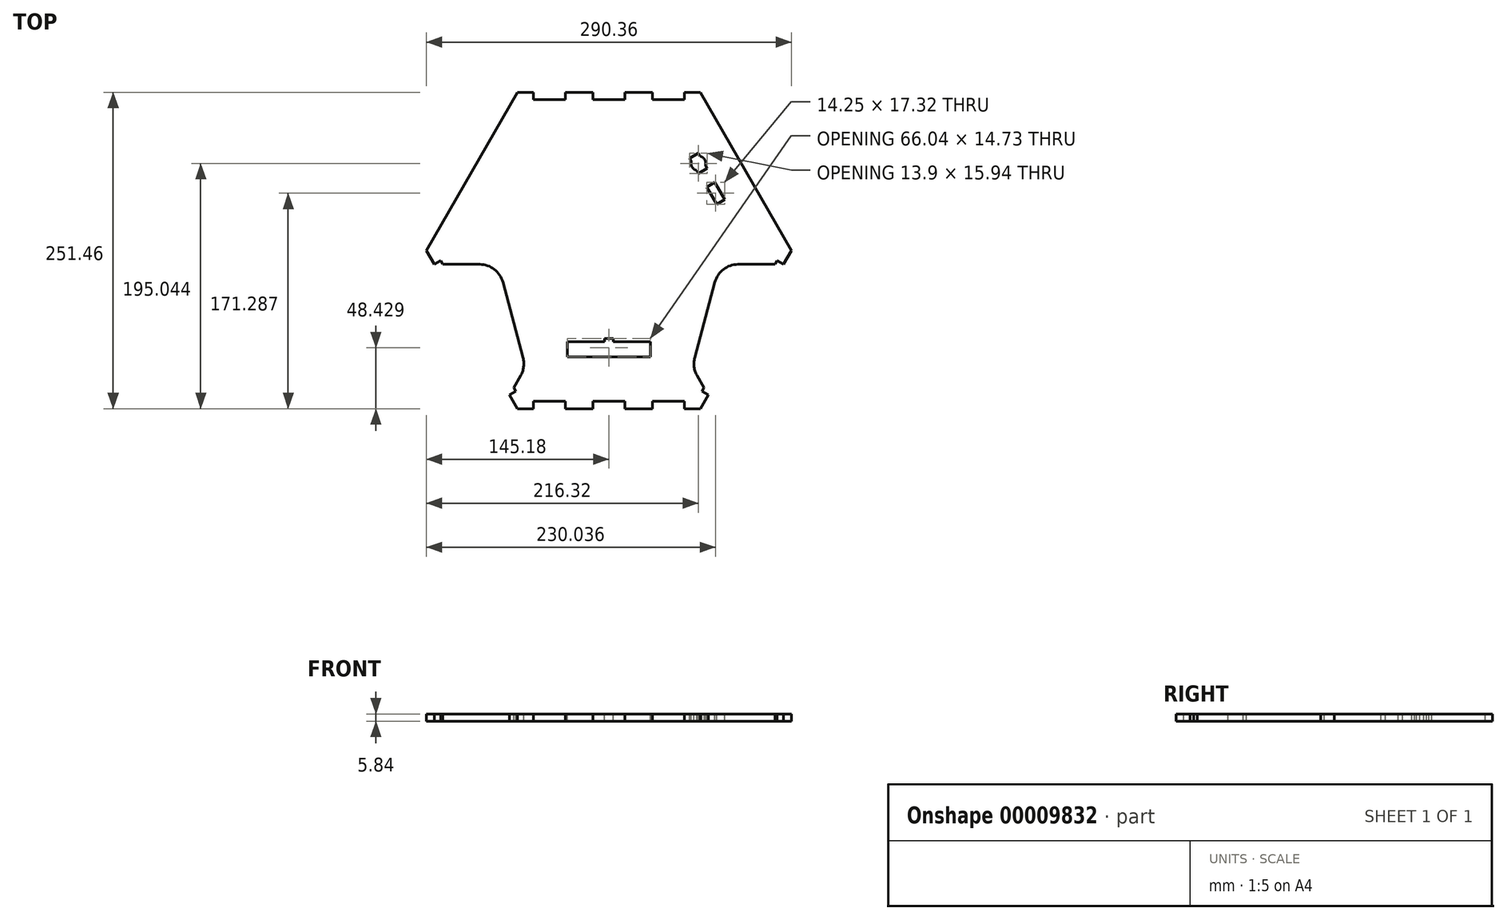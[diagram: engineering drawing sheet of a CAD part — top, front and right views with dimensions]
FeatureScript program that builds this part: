
annotation { "Feature Type Name" : "Feature", "Feature Type Description" : "" }
export const myFeature = defineFeature(function(context is Context, id is Id, definition is map)
    precondition{}
    {
        {
            var Q0;
            Q0=qCreatedBy(makeId("Top.planeOp"),FACE);
            var sketch = newSketch(context, id + "F0", { "sketchPlane" : qUnion([Q0])});
            skCircle(sketch, "E0.cCircle", {"center": v(0, 0) * mm, "radius": 125.73 * mm, "construction": true});
            skLineSegment(sketch, "E0.0", {"start": v(-72.6, 125.73) * mm, "end": v(72.6, 125.73) * mm});
            skLineSegment(sketch, "E0.1", {"start": v(72.6, 125.73) * mm, "end": v(145.18, 0) * mm});
            skLineSegment(sketch, "E0.2", {"start": v(145.18, 0) * mm, "end": v(72.6, -125.73) * mm});
            skLineSegment(sketch, "E0.3", {"start": v(72.6, -125.73) * mm, "end": v(-72.6, -125.73) * mm});
            skLineSegment(sketch, "E0.4", {"start": v(-72.6, -125.73) * mm, "end": v(-145.18, 0) * mm});
            skLineSegment(sketch, "E0.5", {"start": v(-145.18, 0) * mm, "end": v(-72.6, 125.73) * mm});
            skPoint(sketch, "E0.0.midPoint", {"position": v(0, 125.73) * mm});
            skSolve(sketch);
        }
        {
            var Q0;
            Q0=makeQuery(id+"F0.imprint","IMPRINT",FACE,{"disambiguationData":[TD([[makeQuery(id+"F0.imprint","IMPRINT",EDGE,{"derivedFrom":sQuery(id+"F0.wireOp",EDGE,"E0.0")}),-1.0]])]});
            extrude(context, id + "F1", {"entities" : qUnion([Q0]), "depth" : 5.84 * mm});
        }
        {
            var Q0;
            Q0=makeQuery(id+"F1.opExtrude","CAP_FACE",FACE,{"disambiguationData":[OSD([sQuery(id+"F0.wireOp",EDGE,"E0.0"),sQuery(id+"F0.wireOp",EDGE,"E0.1"),sQuery(id+"F0.wireOp",EDGE,"E0.2"),sQuery(id+"F0.wireOp",EDGE,"E0.3"),sQuery(id+"F0.wireOp",EDGE,"E0.4"),sQuery(id+"F0.wireOp",EDGE,"E0.5")])],"isStart":false});
            var sketch = newSketch(context, id + "F2", { "sketchPlane" : qUnion([Q0])});
            skLineSegment(sketch, "E1.bottom", {"start": v(-59.9, -125.73) * mm, "end": v(-34.5, -125.73) * mm});
            skLineSegment(sketch, "E1.top", {"start": v(-59.9, -119.89) * mm, "end": v(-34.5, -119.89) * mm});
            skLineSegment(sketch, "E1.left", {"start": v(-59.9, -125.73) * mm, "end": v(-59.9, -119.89) * mm});
            skLineSegment(sketch, "E1.right", {"start": v(-34.5, -125.73) * mm, "end": v(-34.5, -119.89) * mm});
            skLineSegment(sketch, "E2.bottom", {"start": v(34.5, -125.73) * mm, "end": v(59.9, -125.73) * mm});
            skLineSegment(sketch, "E2.top", {"start": v(34.5, -119.89) * mm, "end": v(59.9, -119.89) * mm});
            skLineSegment(sketch, "E2.left", {"start": v(34.5, -125.73) * mm, "end": v(34.5, -119.89) * mm});
            skLineSegment(sketch, "E2.right", {"start": v(59.9, -125.73) * mm, "end": v(59.9, -119.89) * mm});
            skLineSegment(sketch, "E3.bottom", {"start": v(-12.7, -125.73) * mm, "end": v(12.7, -125.73) * mm});
            skLineSegment(sketch, "E3.top", {"start": v(-12.7, -119.89) * mm, "end": v(12.7, -119.89) * mm});
            skLineSegment(sketch, "E3.left", {"start": v(-12.7, -125.73) * mm, "end": v(-12.7, -119.89) * mm});
            skLineSegment(sketch, "E3.right", {"start": v(12.7, -125.73) * mm, "end": v(12.7, -119.89) * mm});
            skPoint(sketch, "E4", {"position": v(0, -119.89) * mm});
            skLineSegment(sketch, "E5.1.0", {"start": v(138.83, 11) * mm, "end": v(133.77, 8.08) * mm});
            skLineSegment(sketch, "E5.1.1", {"start": v(133.77, 8.08) * mm, "end": v(121.07, 30.07) * mm});
            skLineSegment(sketch, "E5.1.2", {"start": v(138.83, 11) * mm, "end": v(126.13, 33) * mm});
            skLineSegment(sketch, "E5.1.3", {"start": v(126.13, 33) * mm, "end": v(121.07, 30.07) * mm});
            skLineSegment(sketch, "E5.1.4", {"start": v(115.24, 51.87) * mm, "end": v(110.18, 48.95) * mm});
            skLineSegment(sketch, "E5.1.5", {"start": v(110.18, 48.95) * mm, "end": v(97.48, 70.94) * mm});
            skLineSegment(sketch, "E5.1.6", {"start": v(115.24, 51.87) * mm, "end": v(102.54, 73.86) * mm});
            skLineSegment(sketch, "E5.1.7", {"start": v(102.54, 73.86) * mm, "end": v(97.48, 70.94) * mm});
            skLineSegment(sketch, "E5.1.8", {"start": v(86.58, 89.81) * mm, "end": v(73.88, 111.81) * mm});
            skLineSegment(sketch, "E5.1.9", {"start": v(91.64, 92.73) * mm, "end": v(78.94, 114.73) * mm});
            skLineSegment(sketch, "E5.1.10", {"start": v(91.64, 92.73) * mm, "end": v(86.58, 89.81) * mm});
            skLineSegment(sketch, "E5.1.11", {"start": v(78.94, 114.73) * mm, "end": v(73.88, 111.81) * mm});
            skLineSegment(sketch, "E5.2.0", {"start": v(-78.94, 114.73) * mm, "end": v(-73.88, 111.81) * mm});
            skLineSegment(sketch, "E5.2.1", {"start": v(-73.88, 111.81) * mm, "end": v(-86.58, 89.81) * mm});
            skLineSegment(sketch, "E5.2.2", {"start": v(-78.94, 114.73) * mm, "end": v(-91.64, 92.73) * mm});
            skLineSegment(sketch, "E5.2.3", {"start": v(-91.64, 92.73) * mm, "end": v(-86.58, 89.81) * mm});
            skLineSegment(sketch, "E5.2.4", {"start": v(-102.54, 73.86) * mm, "end": v(-97.48, 70.94) * mm});
            skLineSegment(sketch, "E5.2.5", {"start": v(-97.48, 70.94) * mm, "end": v(-110.18, 48.95) * mm});
            skLineSegment(sketch, "E5.2.6", {"start": v(-102.54, 73.86) * mm, "end": v(-115.24, 51.87) * mm});
            skLineSegment(sketch, "E5.2.7", {"start": v(-115.24, 51.87) * mm, "end": v(-110.18, 48.95) * mm});
            skLineSegment(sketch, "E5.2.8", {"start": v(-121.07, 30.07) * mm, "end": v(-133.77, 8.08) * mm});
            skLineSegment(sketch, "E5.2.9", {"start": v(-126.13, 33) * mm, "end": v(-138.83, 11) * mm});
            skLineSegment(sketch, "E5.2.10", {"start": v(-126.13, 33) * mm, "end": v(-121.07, 30.07) * mm});
            skLineSegment(sketch, "E5.2.11", {"start": v(-138.83, 11) * mm, "end": v(-133.77, 8.08) * mm});
            skPoint(sketch, "E5.center", {"position": v(0, 0) * mm});
            skLineSegment(sketch, "E6.1.0", {"start": v(78.94, -114.73) * mm, "end": v(73.88, -111.81) * mm});
            skLineSegment(sketch, "E6.1.1", {"start": v(73.88, -111.81) * mm, "end": v(86.58, -89.81) * mm});
            skLineSegment(sketch, "E6.1.2", {"start": v(78.94, -114.73) * mm, "end": v(91.64, -92.73) * mm});
            skLineSegment(sketch, "E6.1.3", {"start": v(91.64, -92.73) * mm, "end": v(86.58, -89.81) * mm});
            skLineSegment(sketch, "E6.1.4", {"start": v(102.54, -73.86) * mm, "end": v(97.48, -70.94) * mm});
            skLineSegment(sketch, "E6.1.5", {"start": v(97.48, -70.94) * mm, "end": v(110.18, -48.95) * mm});
            skLineSegment(sketch, "E6.1.6", {"start": v(102.54, -73.86) * mm, "end": v(115.24, -51.87) * mm});
            skLineSegment(sketch, "E6.1.7", {"start": v(115.24, -51.87) * mm, "end": v(110.18, -48.95) * mm});
            skLineSegment(sketch, "E6.1.8", {"start": v(126.13, -33) * mm, "end": v(121.07, -30.07) * mm});
            skLineSegment(sketch, "E6.1.9", {"start": v(121.07, -30.07) * mm, "end": v(133.77, -8.08) * mm});
            skLineSegment(sketch, "E6.1.10", {"start": v(126.13, -33) * mm, "end": v(138.83, -11) * mm});
            skLineSegment(sketch, "E6.1.11", {"start": v(138.83, -11) * mm, "end": v(133.77, -8.08) * mm});
            skLineSegment(sketch, "E6.3.0", {"start": v(59.9, 125.73) * mm, "end": v(59.9, 119.89) * mm});
            skLineSegment(sketch, "E6.3.1", {"start": v(59.9, 119.89) * mm, "end": v(34.5, 119.89) * mm});
            skLineSegment(sketch, "E6.3.2", {"start": v(59.9, 125.73) * mm, "end": v(34.5, 125.73) * mm});
            skLineSegment(sketch, "E6.3.3", {"start": v(34.5, 125.73) * mm, "end": v(34.5, 119.89) * mm});
            skLineSegment(sketch, "E6.3.4", {"start": v(12.7, 125.73) * mm, "end": v(12.7, 119.89) * mm});
            skLineSegment(sketch, "E6.3.5", {"start": v(12.7, 119.89) * mm, "end": v(-12.7, 119.89) * mm});
            skLineSegment(sketch, "E6.3.6", {"start": v(12.7, 125.73) * mm, "end": v(-12.7, 125.73) * mm});
            skLineSegment(sketch, "E6.3.7", {"start": v(-12.7, 125.73) * mm, "end": v(-12.7, 119.89) * mm});
            skLineSegment(sketch, "E6.3.8", {"start": v(-34.5, 125.73) * mm, "end": v(-34.5, 119.89) * mm});
            skLineSegment(sketch, "E6.3.9", {"start": v(-34.5, 119.89) * mm, "end": v(-59.9, 119.89) * mm});
            skLineSegment(sketch, "E6.3.10", {"start": v(-34.5, 125.73) * mm, "end": v(-59.9, 125.73) * mm});
            skLineSegment(sketch, "E6.3.11", {"start": v(-59.9, 125.73) * mm, "end": v(-59.9, 119.89) * mm});
            skLineSegment(sketch, "E6.5.0", {"start": v(-138.83, -11) * mm, "end": v(-133.77, -8.08) * mm});
            skLineSegment(sketch, "E6.5.1", {"start": v(-133.77, -8.08) * mm, "end": v(-121.07, -30.07) * mm});
            skLineSegment(sketch, "E6.5.2", {"start": v(-138.83, -11) * mm, "end": v(-126.13, -33) * mm});
            skLineSegment(sketch, "E6.5.3", {"start": v(-126.13, -33) * mm, "end": v(-121.07, -30.07) * mm});
            skLineSegment(sketch, "E6.5.4", {"start": v(-115.24, -51.87) * mm, "end": v(-110.18, -48.95) * mm});
            skLineSegment(sketch, "E6.5.5", {"start": v(-110.18, -48.95) * mm, "end": v(-97.48, -70.94) * mm});
            skLineSegment(sketch, "E6.5.6", {"start": v(-115.24, -51.87) * mm, "end": v(-102.54, -73.86) * mm});
            skLineSegment(sketch, "E6.5.7", {"start": v(-102.54, -73.86) * mm, "end": v(-97.48, -70.94) * mm});
            skLineSegment(sketch, "E6.5.8", {"start": v(-91.64, -92.73) * mm, "end": v(-86.58, -89.81) * mm});
            skLineSegment(sketch, "E6.5.9", {"start": v(-86.58, -89.81) * mm, "end": v(-73.88, -111.81) * mm});
            skLineSegment(sketch, "E6.5.10", {"start": v(-91.64, -92.73) * mm, "end": v(-78.94, -114.73) * mm});
            skLineSegment(sketch, "E6.5.11", {"start": v(-78.94, -114.73) * mm, "end": v(-73.88, -111.81) * mm});
            skPoint(sketch, "E7", {"position": v(0, -125.73) * mm});
            skSolve(sketch);
        }
        {
            var Q0;
            Q0=makeQuery(id+"F2.imprint","IMPRINT",FACE,{"disambiguationData":[TD([[makeQuery(id+"F2.imprint","IMPRINT",EDGE,{"derivedFrom":sQuery(id+"F2.wireOp",EDGE,"E1.bottom")}),-1.0]])]});
            var Q1;
            Q1=makeQuery(id+"F2.imprint","IMPRINT",FACE,{"disambiguationData":[TD([[makeQuery(id+"F2.imprint","IMPRINT",EDGE,{"derivedFrom":sQuery(id+"F2.wireOp",EDGE,"E3.bottom")}),-1.0]])]});
            var Q2;
            Q2=makeQuery(id+"F2.imprint","IMPRINT",FACE,{"disambiguationData":[TD([[makeQuery(id+"F2.imprint","IMPRINT",EDGE,{"derivedFrom":sQuery(id+"F2.wireOp",EDGE,"E2.bottom")}),-1.0]])]});
            var Q3;
            Q3=makeQuery(id+"F2.imprint","IMPRINT",FACE,{"disambiguationData":[TD([[makeQuery(id+"F2.imprint","IMPRINT",EDGE,{"derivedFrom":sQuery(id+"F2.wireOp",EDGE,"E6.5.8")}),-1.0]])]});
            var Q4;
            Q4=makeQuery(id+"F2.imprint","IMPRINT",FACE,{"disambiguationData":[TD([[makeQuery(id+"F2.imprint","IMPRINT",EDGE,{"derivedFrom":sQuery(id+"F2.wireOp",EDGE,"E6.5.4")}),-1.0]])]});
            var Q5;
            Q5=makeQuery(id+"F2.imprint","IMPRINT",FACE,{"disambiguationData":[TD([[makeQuery(id+"F2.imprint","IMPRINT",EDGE,{"derivedFrom":sQuery(id+"F2.wireOp",EDGE,"E6.5.0")}),-1.0]])]});
            var Q6;
            Q6=makeQuery(id+"F2.imprint","IMPRINT",FACE,{"disambiguationData":[TD([[makeQuery(id+"F2.imprint","IMPRINT",EDGE,{"derivedFrom":sQuery(id+"F2.wireOp",EDGE,"E5.2.10")}),-1.0]])]});
            var Q7;
            Q7=makeQuery(id+"F2.imprint","IMPRINT",FACE,{"disambiguationData":[TD([[makeQuery(id+"F2.imprint","IMPRINT",EDGE,{"derivedFrom":sQuery(id+"F2.wireOp",EDGE,"E5.2.4")}),-1.0]])]});
            var Q8;
            Q8=makeQuery(id+"F2.imprint","IMPRINT",FACE,{"disambiguationData":[TD([[makeQuery(id+"F2.imprint","IMPRINT",EDGE,{"derivedFrom":sQuery(id+"F2.wireOp",EDGE,"E5.2.0")}),-1.0]])]});
            var Q9;
            Q9=makeQuery(id+"F2.imprint","IMPRINT",FACE,{"disambiguationData":[TD([[makeQuery(id+"F2.imprint","IMPRINT",EDGE,{"derivedFrom":sQuery(id+"F2.wireOp",EDGE,"E6.3.8")}),-1.0]])]});
            var Q10;
            Q10=makeQuery(id+"F2.imprint","IMPRINT",FACE,{"disambiguationData":[TD([[makeQuery(id+"F2.imprint","IMPRINT",EDGE,{"derivedFrom":sQuery(id+"F2.wireOp",EDGE,"E6.3.4")}),-1.0]])]});
            var Q11;
            Q11=makeQuery(id+"F2.imprint","IMPRINT",FACE,{"disambiguationData":[TD([[makeQuery(id+"F2.imprint","IMPRINT",EDGE,{"derivedFrom":sQuery(id+"F2.wireOp",EDGE,"E6.3.0")}),-1.0]])]});
            var Q12;
            Q12=makeQuery(id+"F2.imprint","IMPRINT",FACE,{"disambiguationData":[TD([[makeQuery(id+"F2.imprint","IMPRINT",EDGE,{"derivedFrom":sQuery(id+"F2.wireOp",EDGE,"E5.1.10")}),-1.0]])]});
            var Q13;
            Q13=makeQuery(id+"F2.imprint","IMPRINT",FACE,{"disambiguationData":[TD([[makeQuery(id+"F2.imprint","IMPRINT",EDGE,{"derivedFrom":sQuery(id+"F2.wireOp",EDGE,"E5.1.4")}),-1.0]])]});
            var Q14;
            Q14=makeQuery(id+"F2.imprint","IMPRINT",FACE,{"disambiguationData":[TD([[makeQuery(id+"F2.imprint","IMPRINT",EDGE,{"derivedFrom":sQuery(id+"F2.wireOp",EDGE,"E5.1.0")}),-1.0]])]});
            var Q15;
            Q15=makeQuery(id+"F2.imprint","IMPRINT",FACE,{"disambiguationData":[TD([[makeQuery(id+"F2.imprint","IMPRINT",EDGE,{"derivedFrom":sQuery(id+"F2.wireOp",EDGE,"E6.1.8")}),-1.0]])]});
            var Q16;
            Q16=makeQuery(id+"F2.imprint","IMPRINT",FACE,{"disambiguationData":[TD([[makeQuery(id+"F2.imprint","IMPRINT",EDGE,{"derivedFrom":sQuery(id+"F2.wireOp",EDGE,"E6.1.4")}),-1.0]])]});
            var Q17;
            Q17=makeQuery(id+"F2.imprint","IMPRINT",FACE,{"disambiguationData":[TD([[makeQuery(id+"F2.imprint","IMPRINT",EDGE,{"derivedFrom":sQuery(id+"F2.wireOp",EDGE,"E6.1.0")}),-1.0]])]});
            var Q18;
            Q18=makeQuery(id+"F1.opExtrude","CAP_FACE",FACE,{"disambiguationData":[OSD([sQuery(id+"F0.wireOp",EDGE,"E0.0"),sQuery(id+"F0.wireOp",EDGE,"E0.1"),sQuery(id+"F0.wireOp",EDGE,"E0.2"),sQuery(id+"F0.wireOp",EDGE,"E0.3"),sQuery(id+"F0.wireOp",EDGE,"E0.4"),sQuery(id+"F0.wireOp",EDGE,"E0.5")])],"isStart":true});
            extrude(context, id + "F3", {"entities" : qUnion([Q0, Q1, Q2, Q3, Q4, Q5, Q6, Q7, Q8, Q9, Q10, Q11, Q12, Q13, Q14, Q15, Q16, Q17]), "operationType" : NewBodyOperationType.REMOVE, "endBound" : BoundingType.UP_TO_SURFACE, "oppositeDirection" : true, "endBoundEntityFace" : qUnion([Q18]), "depth" : 25.4 * mm});
        }
        {
            var Q0;
            Q0=makeQuery(id+"F2.imprint","IMPRINT",FACE,{"disambiguationData":[TD([[makeQuery(id+"F2.imprint","IMPRINT",EDGE,{"derivedFrom":sQuery(id+"F2.wireOp",EDGE,"E1.top")}),1.0]])]});
            var sketch = newSketch(context, id + "F4", { "sketchPlane" : qUnion([Q0])});
            skLineSegment(sketch, "E8.bottom", {"start": v(-33.02, -72.47) * mm, "end": v(33.02, -72.47) * mm});
            skLineSegment(sketch, "E8.top", {"start": v(-33.02, -84.67) * mm, "end": v(33.02, -84.67) * mm});
            skLineSegment(sketch, "E8.left", {"start": v(-33.02, -72.47) * mm, "end": v(-33.02, -84.67) * mm});
            skLineSegment(sketch, "E8.right", {"start": v(33.02, -72.47) * mm, "end": v(33.02, -84.67) * mm});
            skLineSegment(sketch, "E9", {"start": v(-3.56, -72.47) * mm, "end": v(-3.56, -69.93) * mm});
            skLineSegment(sketch, "E10", {"start": v(-3.56, -69.93) * mm, "end": v(3.56, -69.93) * mm});
            skLineSegment(sketch, "E11", {"start": v(3.56, -69.93) * mm, "end": v(3.56, -72.47) * mm});
            skPoint(sketch, "E12", {"position": v(0, -72.47) * mm});
            skPoint(sketch, "E13", {"position": v(0, -69.93) * mm});
            skPoint(sketch, "E14", {"position": v(33.02, -78.57) * mm});
            skSolve(sketch);
        }
        {
            var Q0;
            Q0=makeQuery(id+"F4.imprint","IMPRINT",FACE,{"disambiguationData":[TD([[makeQuery(id+"F4.imprint","IMPRINT",EDGE,{"derivedFrom":sQuery(id+"F4.wireOp",EDGE,"E8.top")}),1.0]])]});
            var Q1;
            {var subQ1=sQuery(id+"F4.wireOp",EDGE,"E9");Q1=makeQuery(id+"F4.imprint","IMPRINT",FACE,{"disambiguationData":[TD([[makeQuery(id+"F4.imprint","IMPRINT",EDGE,{"derivedFrom":subQ1}),-1.0]])]});}
            var Q2;
            Q2=makeQuery(id+"F1.opExtrude","CAP_FACE",FACE,{"disambiguationData":[OSD([sQuery(id+"F0.wireOp",EDGE,"E0.0"),sQuery(id+"F0.wireOp",EDGE,"E0.1"),sQuery(id+"F0.wireOp",EDGE,"E0.2"),sQuery(id+"F0.wireOp",EDGE,"E0.3"),sQuery(id+"F0.wireOp",EDGE,"E0.4"),sQuery(id+"F0.wireOp",EDGE,"E0.5")])],"isStart":true});
            extrude(context, id + "F5", {"entities" : qUnion([Q0, Q1]), "operationType" : NewBodyOperationType.REMOVE, "endBound" : BoundingType.UP_TO_SURFACE, "oppositeDirection" : true, "endBoundEntityFace" : qUnion([Q2]), "depth" : 25.4 * mm});
        }
        {
            var Q0;
            Q0=makeQuery(id+"F2.imprint","IMPRINT",FACE,{"disambiguationData":[TD([[makeQuery(id+"F2.imprint","IMPRINT",EDGE,{"derivedFrom":sQuery(id+"F2.wireOp",EDGE,"E1.top")}),1.0]])]});
            var sketch = newSketch(context, id + "F6", { "sketchPlane" : qUnion([Q0])});
            skLineSegment(sketch, "E15", {"start": v(-78.94, -114.73) * mm, "end": v(-70.18, -99.56) * mm});
            skLineSegment(sketch, "E16", {"start": v(-68.27, -85.12) * mm, "end": v(-84.26, -25.14) * mm});
            skLineSegment(sketch, "E17", {"start": v(-102.67, -11) * mm, "end": v(-138.83, -11) * mm});
            skLineSegment(sketch, "E18", {"start": v(-138.83, -11) * mm, "end": v(-78.94, -114.73) * mm});
            skPoint(sketch, "E19.visualSharp", {"position": v(-66.24, -92.73) * mm});
            skArc(sketch, "E19.filletArc", {"start": v(-70.18, -99.56) * mm, "mid": v(-67.8, -92.53) * mm, "end": v(-68.27, -85.12) * mm});
            skPoint(sketch, "E20.visualSharp", {"position": v(-88.03, -11) * mm});
            skArc(sketch, "E20.filletArc", {"start": v(-84.26, -25.14) * mm, "mid": v(-91.06, -14.94) * mm, "end": v(-102.67, -11) * mm});
            skSolve(sketch);
        }
        {
            var Q0;
            Q0 = qSketchRegion(id + "F6", true);
            extrude(context, id + "F7", {"entities" : qUnion([Q0]), "operationType" : NewBodyOperationType.REMOVE, "oppositeDirection" : true, "depth" : 25.4 * mm});
        }
        {
            var Q0;
            Q0=makeQuery(id+"F2.imprint","IMPRINT",FACE,{"disambiguationData":[TD([[makeQuery(id+"F2.imprint","IMPRINT",EDGE,{"derivedFrom":sQuery(id+"F2.wireOp",EDGE,"E1.top")}),1.0]])]});
            var sketch = newSketch(context, id + "F8", { "sketchPlane" : qUnion([Q0])});
            skLineSegment(sketch, "E21", {"start": v(138.83, -11) * mm, "end": v(102.67, -11) * mm});
            skLineSegment(sketch, "E22", {"start": v(84.26, -25.14) * mm, "end": v(68.27, -85.12) * mm});
            skLineSegment(sketch, "E23", {"start": v(70.18, -99.56) * mm, "end": v(78.94, -114.73) * mm});
            skLineSegment(sketch, "E24", {"start": v(78.94, -114.73) * mm, "end": v(138.83, -11) * mm});
            skPoint(sketch, "E25.visualSharp", {"position": v(88.03, -11) * mm});
            skArc(sketch, "E25.filletArc", {"start": v(102.67, -11) * mm, "mid": v(91.06, -14.94) * mm, "end": v(84.26, -25.14) * mm});
            skPoint(sketch, "E26.visualSharp", {"position": v(66.24, -92.73) * mm});
            skArc(sketch, "E26.filletArc", {"start": v(68.27, -85.12) * mm, "mid": v(67.8, -92.53) * mm, "end": v(70.18, -99.56) * mm});
            skSolve(sketch);
        }
        {
            var Q0;
            Q0 = qSketchRegion(id + "F8", true);
            extrude(context, id + "F9", {"entities" : qUnion([Q0]), "operationType" : NewBodyOperationType.REMOVE, "oppositeDirection" : true, "depth" : 25.4 * mm});
        }
        {
            var Q0;
            Q0=makeQuery(id+"F2.imprint","IMPRINT",FACE,{"disambiguationData":[TD([[makeQuery(id+"F2.imprint","IMPRINT",EDGE,{"derivedFrom":sQuery(id+"F2.wireOp",EDGE,"E1.top")}),1.0]])]});
            var sketch = newSketch(context, id + "F10", { "sketchPlane" : qUnion([Q0])});
            skLineSegment(sketch, "E27.bottom", {"start": v(64.2, 73.22) * mm, "end": v(71.23, 77.28) * mm});
            skLineSegment(sketch, "E27.top", {"start": v(71.05, 61.34) * mm, "end": v(78.09, 65.4) * mm});
            skLineSegment(sketch, "E27.left", {"start": v(64.2, 73.22) * mm, "end": v(71.05, 61.34) * mm});
            skLineSegment(sketch, "E27.right", {"start": v(71.23, 77.28) * mm, "end": v(78.09, 65.4) * mm});
            skPoint(sketch, "E28", {"position": v(67.62, 67.28) * mm});
            skCircle(sketch, "E29", {"center": v(71.14, 69.31) * mm, "radius": 5.84 * mm});
            skPoint(sketch, "E30", {"position": v(67.71, 75.25) * mm});
            skLineSegment(sketch, "E31", {"start": v(67.62, 67.28) * mm, "end": v(74.66, 71.35) * mm, "construction": true});
            skLineSegment(sketch, "E32", {"start": v(67.71, 75.25) * mm, "end": v(74.57, 63.37) * mm, "construction": true});
            skSolve(sketch);
        }
        {
            var Q0;
            Q0 = qSketchRegion(id + "F10", true);
            extrude(context, id + "F11", {"entities" : qUnion([Q0]), "operationType" : NewBodyOperationType.REMOVE, "oppositeDirection" : true, "depth" : 25.4 * mm});
        }
        {
            var Q0;
            Q0=makeQuery(id+"F1.opExtrude","CAP_FACE",FACE,{"disambiguationData":[OSD([sQuery(id+"F0.wireOp",EDGE,"E0.0"),sQuery(id+"F0.wireOp",EDGE,"E0.1"),sQuery(id+"F0.wireOp",EDGE,"E0.2"),sQuery(id+"F0.wireOp",EDGE,"E0.3"),sQuery(id+"F0.wireOp",EDGE,"E0.4"),sQuery(id+"F0.wireOp",EDGE,"E0.5")])],"isStart":false});
            var sketch = newSketch(context, id + "F12", { "sketchPlane" : qUnion([Q0])});
            skLineSegment(sketch, "E33.bottom", {"start": v(77.73, 50.53) * mm, "end": v(84.1, 54.22) * mm});
            skLineSegment(sketch, "E33.top", {"start": v(85.6, 36.9) * mm, "end": v(91.98, 40.58) * mm});
            skLineSegment(sketch, "E33.left", {"start": v(77.73, 50.53) * mm, "end": v(85.6, 36.9) * mm});
            skLineSegment(sketch, "E33.right", {"start": v(84.1, 54.22) * mm, "end": v(91.98, 40.58) * mm});
            skPoint(sketch, "E34", {"position": v(74.57, 63.37) * mm});
            skPoint(sketch, "E35", {"position": v(80.92, 52.38) * mm});
            skLineSegment(sketch, "E36", {"start": v(80.92, 52.38) * mm, "end": v(74.57, 63.37) * mm, "construction": true});
            skSolve(sketch);
        }
        {
            var Q0;
            Q0=makeQuery(id+"F12.imprint","IMPRINT",FACE,{"disambiguationData":[TD([[makeQuery(id+"F12.imprint","IMPRINT",EDGE,{"derivedFrom":sQuery(id+"F12.wireOp",EDGE,"E33.bottom")}),-1.0]])]});
            var Q1;
            Q1=makeQuery(id+"F1.opExtrude","CAP_FACE",FACE,{"disambiguationData":[OSD([sQuery(id+"F0.wireOp",EDGE,"E0.0"),sQuery(id+"F0.wireOp",EDGE,"E0.1"),sQuery(id+"F0.wireOp",EDGE,"E0.2"),sQuery(id+"F0.wireOp",EDGE,"E0.3"),sQuery(id+"F0.wireOp",EDGE,"E0.4"),sQuery(id+"F0.wireOp",EDGE,"E0.5")])],"isStart":true});
            extrude(context, id + "F13", {"entities" : qUnion([Q0]), "operationType" : NewBodyOperationType.REMOVE, "endBound" : BoundingType.UP_TO_SURFACE, "oppositeDirection" : true, "endBoundEntityFace" : qUnion([Q1]), "depth" : 25.4 * mm});
        }
    });
